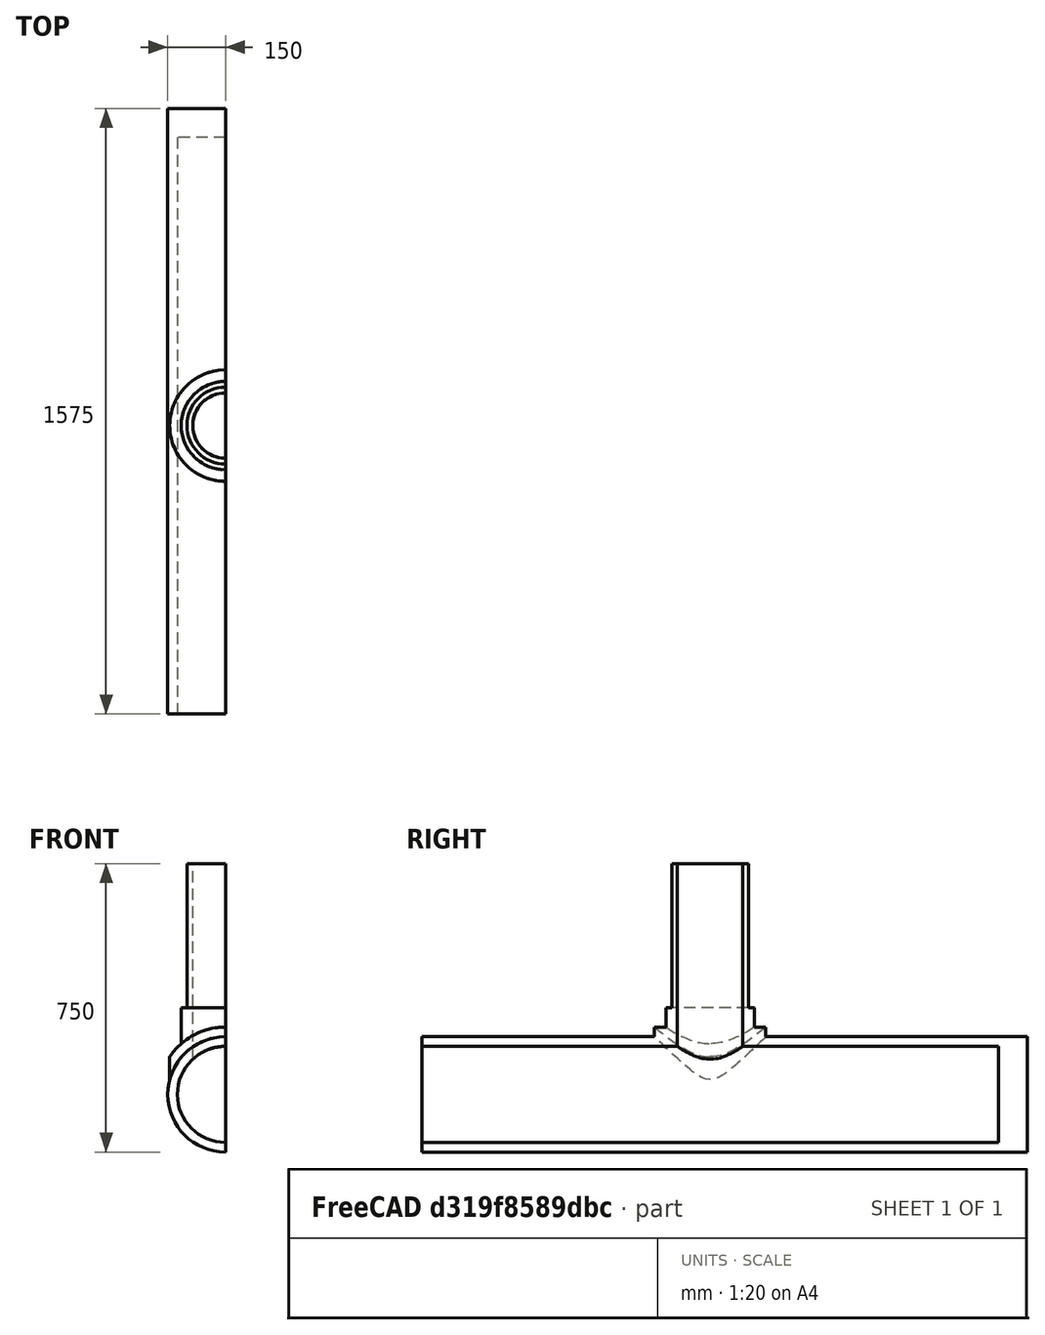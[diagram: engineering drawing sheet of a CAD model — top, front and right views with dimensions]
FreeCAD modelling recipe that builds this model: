
FCSTD DOCUMENT  (FreeCAD 0.16RUnknown)
Label: T-pipe static FEM model
License: All rights reserved
LicenseURL: http://en.wikipedia.org/wiki/All_rights_reserved
objects: Part::Cylinder×9, Part::Cut×6, Fem::ConstraintDisplacement×3, Part::Box×2, Part::MultiFuse×2, Fem::FemSolverObjectPython×1, Fem::FemMeshShapeNetgenObject×1, App::MaterialObjectPython×1, Fem::ConstraintPlaneRotation×1, Fem::ConstraintPressure×1, Fem::FemAnalysisPython×1
note: 19 computed .brp shape members not serialized (recipe doc carries the construction recipe); baked Part::Feature solids carry a one-line shape summary decoded from their .brp

FEATURE [Part::Cylinder] Cylinder
  Angle = 360
  Height = 600
  Radius = 100
FEATURE [Part::Cylinder] Cylinder001
  Angle = 360
  Height = 1500
  Placement = pos=(0,750,0) rot=(1,0,0;1.5708rad)
  Radius = 150
FEATURE [Part::Cylinder] Cylinder002
  Angle = 360
  Height = 225
  Radius = 115
FEATURE [Part::Cylinder] Cylinder003
  Angle = 360
  Height = 400
  Placement = pos=(0,200,0) rot=(1,0,0;1.5708rad)
  Radius = 175
FEATURE [Part::Cylinder] Cylinder004
  Angle = 360
  Height = 600
  Radius = 145
FEATURE [Part::Cylinder] Cylinder005
  Angle = 360
  Height = 600
  Radius = 300
FEATURE [Part::Cut] Cut
  Base = -> Cylinder005
  Tool = -> Cylinder004
FEATURE [Part::Cut] Cut001
  Base = -> Cylinder003
  Tool = -> Cut
FEATURE [Part::Box] Box  label="Cube"
  Height = 500
  Length = 500
  Placement = pos=(-226,-279,-480) rot=(0,0,1;0rad)
  Width = 500
FEATURE [Part::Cut] Cut002
  Base = -> Cut001
  Tool = -> Box
FEATURE [Part::MultiFuse] Fusion
  Shapes = -> [Cut002,Cylinder002,Cylinder001,Cylinder]
FEATURE [Part::Cylinder] Cylinder006
  Angle = 360
  Height = 600
  Radius = 85
FEATURE [Part::Cut] Cut003
  Base = -> Fusion
  Tool = -> Cylinder006
FEATURE [Part::Cylinder] Cylinder007
  Angle = 360
  Height = 1500
  Placement = pos=(0,750,0) rot=(1,0,0;1.5708rad)
  Radius = 125
FEATURE [Part::Cut] Cut004
  Base = -> Cut003
  Tool = -> Cylinder007
FEATURE [Part::Cylinder] Cylinder008
  Angle = 360
  Height = 75
  Placement = pos=(0,825,0) rot=(1,0,0;1.5708rad)
  Radius = 150
FEATURE [Part::Box] Box001  label="Cube001"
  Height = 1000
  Length = 500
  Placement = pos=(0,-815,-274) rot=(0,0,1;0rad)
  Width = 1800
FEATURE [Part::MultiFuse] Fusion001
  Shapes = -> [Cut004,Cylinder008]
FEATURE [Part::Cut] Cut005
  Base = -> Fusion001
  Tool = -> Box001
FEATURE [Fem::FemSolverObjectPython] CalculiX  # FEM object (typed FeaturePython)
  AnalysisType = 0
  EigenmodeHighLimit = 1000000
  EigenmodeLowLimit = 0
  EndTime = 1
  InitialTimeStep = 0.01
  MatrixSolverType = 0
  Maxiterations = 2000
  NonLinearGeometry = false
  NumCpus = 6
  NumberOfEigenmodes = 10
  SolverType = FemSolverCalculix
  SteadyState = true
FEATURE [Fem::FemMeshShapeNetgenObject] Cut005_Mesh
  Fineness = 2
  GrowthRate = 0.3
  MaxSize = 1000
  NbSegsPerEdge = 1
  NbSegsPerRadius = 2
  Optimize = true
  SecondOrder = true
  Shape = -> Cut005
FEATURE [App::MaterialObjectPython] MechanicalMaterial  # material (typed FeaturePython)
  Material = Density=7900.0 kg/m^3,+10 more (map truncated)
FEATURE [Fem::ConstraintPlaneRotation] FemConstraintPlaneRotation
  NormalDirection = (0,1,0)
  Normals = (8) [(0,1,-2.22045e-16),(0,1,-2.22045e-16),(0,1,-2.22045e-16),(0,1,-2.22045e-16),(0,1,-2.22045e-16),(0,1,-2.22045e-16),(0,1,-2.22045e-16),+1 more]
  Points = (8) [(0,825,-150),(-100,825,-50),(-50,825,-50),(0,825,-50),(-100,825,50),(-50,825,50),(0,825,50),(0,825,150)]
  References = -> [Cut005]
  Scale = 16
FEATURE [Fem::ConstraintPressure] FemConstraintPressure
  NormalDirection = (1,0,-1.159e-09)
  Normals = (44) [(-2.31845e-09,-2.22045e-16,-1),(0.866025,-1.11022e-16,-0.5),(0.866025,1.11022e-16,0.5),(1.83697e-16,2.22045e-16,1),(-2.31845e-09,-2.22045e-16,-1),+39 more]
  Points = (44) [(2.89807e-07,750,125),(-108.253,750,62.5),(-108.253,750,-62.5),(-2.29621e-14,750,-125),(2.89807e-07,450,125),(-108.253,450,62.5),(-108.253,450,-62.5),+37 more]
  Pressure = 9
  References = -> [Cut005]
  Scale = 14
FEATURE [Fem::ConstraintDisplacement] FemConstraintDisplacement
  NormalDirection = (1,0,0)
  Normals = (8) [(1,0,0),(1,0,0),(1,0,0),(1,0,0),(1,0,0),(1,0,0),(1,0,0),(1,0,0)]
  Points = (8) [(0,-750,125),(0,825,-150),(0,825,100),(0,510,-150),(0,195,-150),(0,-120,-150),(0,-435,-150),(0,-750,-150)]
  References = -> [Cut005]
  Scale = 35
  rotxFix = false
  rotxFree = true
  rotyFix = false
  rotyFree = true
  rotzFix = false
  rotzFree = true
  xDisplacement = 0
  xFix = true
  xFree = false
  xRotation = 0
  yDisplacement = 0
  yFix = false
  yFree = true
  yRotation = 0
  zDisplacement = 0
  zFix = false
  zFree = true
  zRotation = 0
FEATURE [Fem::ConstraintDisplacement] FemConstraintDisplacement001
  NormalDirection = (0,-1,0)
  Normals = (2) [(0,-1,2.22045e-16),(0,-1,2.22045e-16)]
  Points = (2) [(0,-750,-150),(0,-750,150)]
  References = -> [Cut005]
  Scale = 16
  rotxFix = false
  rotxFree = true
  rotyFix = false
  rotyFree = true
  rotzFix = false
  rotzFree = true
  xDisplacement = 0
  xFix = false
  xFree = true
  xRotation = 0
  yDisplacement = 0
  yFix = true
  yFree = false
  yRotation = 0
  zDisplacement = 0
  zFix = false
  zFree = true
  zRotation = 0
FEATURE [Fem::ConstraintDisplacement] FemConstraintDisplacement002
  NormalDirection = (0,0,1)
  Normals = (2) [(0,0,1),(0,0,1)]
  Points = (2) [(0,-100,600),(0,100,600)]
  References = -> [Cut005]
  Scale = 13
  rotxFix = false
  rotxFree = true
  rotyFix = false
  rotyFree = true
  rotzFix = false
  rotzFree = true
  xDisplacement = 0
  xFix = false
  xFree = true
  xRotation = 0
  yDisplacement = 0
  yFix = false
  yFree = true
  yRotation = 0
  zDisplacement = 0
  zFix = true
  zFree = false
  zRotation = 0
FEATURE [Fem::FemAnalysisPython] MechanicalAnalysis  # FEM object (typed FeaturePython)
  Member = -> [CalculiX,Cut005_Mesh,MechanicalMaterial,FemConstraintPlaneRotation,FemConstraintPressure,FemConstraintDisplacement,FemConstraintDisplacement001,FemConstraintDisplacement002]
